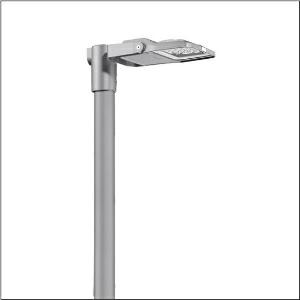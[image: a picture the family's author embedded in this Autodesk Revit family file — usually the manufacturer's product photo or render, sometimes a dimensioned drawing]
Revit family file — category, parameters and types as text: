
# Revit family: floodlight_fl_21_iq_micro___pl64_5xa7762a4e3a_dfd9
name_source: partatom
category: Lighting Fixtures
units: mm (PartAtom-declared; Revit-internal decimal feet)

## family parameters
Cut with Voids When Loaded = No
Host = Face
Light Source = No
Part Type = Normal
Room Calculation Point = No
Round Connector Dimension = Use Diameter
Shared = No

## types (1)
- --- (1 x LED, 2980 lm, 23.1 W, 4000K)
    Apparent Load = 23 VA
    CIE Flux Codes = 28 80 98 100 100
    Color Rendering = 70
    Color Temperature = 4000K
    Default Elevation = 1800 mm
    Description = Floodlight FL 21 iQ micro, floodlight, primary light control with lens, of PMMA, primary optical cover: protective disc, of toughened safety glass, transparent, light distribution: PL64, light emission: direct distribution, installation type: surface-mounted, LED, High Power LED, rated luminous flux: 2.980lm, luminous efficacy: 129lm/W, light colour: 740, colour temperature: 4000K, control: Auto-Match, Temp-Guard, Night-Set, Smart-Wire, Desk-Remote (wireless, voltage-free reading and setting of iQ features in the workshop via application-optimized NFC function/RFID function), optimised constant luminous flux control (CLO 2.0), Street-Remote, with terminal, 6-pole, mains connection: 220..240V, AC, 50/60Hz, start of lifetime: 23W, end of service life: 24W, reduction: 11W, luminaire housing, of diecast aluminium, powder-coated, Siteco® metallic grey (DB 702S), corrosivity category C5 mid according to DIN EN ISO 12944, sealing non-destructively replaceable, please order mast flange separately, mast bracket, of steel, galvanised, powder-coated, Siteco® metallic grey (DB 702S), protection rating (complete): IP66, insulation class (complete): insulation class II (safety insulation), certification: CE, ENEC, VDE, protection symbol: D, impact resistance: IK07, permissible operating ambient temperature: -40..+40°C, permissible operating ambient temperature for outdoor applications: -40..+50°C, standard: DIN EN 12944, LABS conformity tested according to VDMA 24364:2018-05, packaging unit: 1 piece

Light Distribution: PL64
    Height = 65 mm
    Lamp = 1 x LED
    Lamp Light Flux = 2980 lm
    Lamp Power = 23.1 W
    Lamp count = 1
    Length = 312 mm
    Luminous efficacy = 129 lm/W
    Manufacturer = Siteco
    ModVariant = No
    Model = 5XA7762A4E3A
    Number of Poles = 1
    OnlyDefault = Yes
    Power Factor = 1
    Product Name = Floodlight FL 21 iQ micro | PL64
    Product group = floodlight | pylon annexe
    ProductGroupID = 6200
    Protection Class = Protection class II
    Protection Degree = IP 66
    RLX_Detail_Level = 1
    RLX_Emergency_Light_Flux = 0 lm
    RLX_Emergency_Type = 0
    RLX_Emergency_Type_DB = No
    RlxData = <blob elided: 101657 chars, md5=85813fac>
    Socket = socket
    Standby Power = 0 W
    System Light Flux = 2980 lm
    System Power = 23 W
    Type Comments = factory setting: luminous flux: 100 % | dim-lin: 254 | 455 mA
    Type Image = l_1007121.jpg
    URL = http://relux.com
    VarID = @adj_113575
    Voltage = 0 V
    Weight = 0.00 kg
    Width = 230 mm

## geometry (parser evidence)
native form markers: Blend x4, Sweep x12
no freeform markers — native parametric forms only
